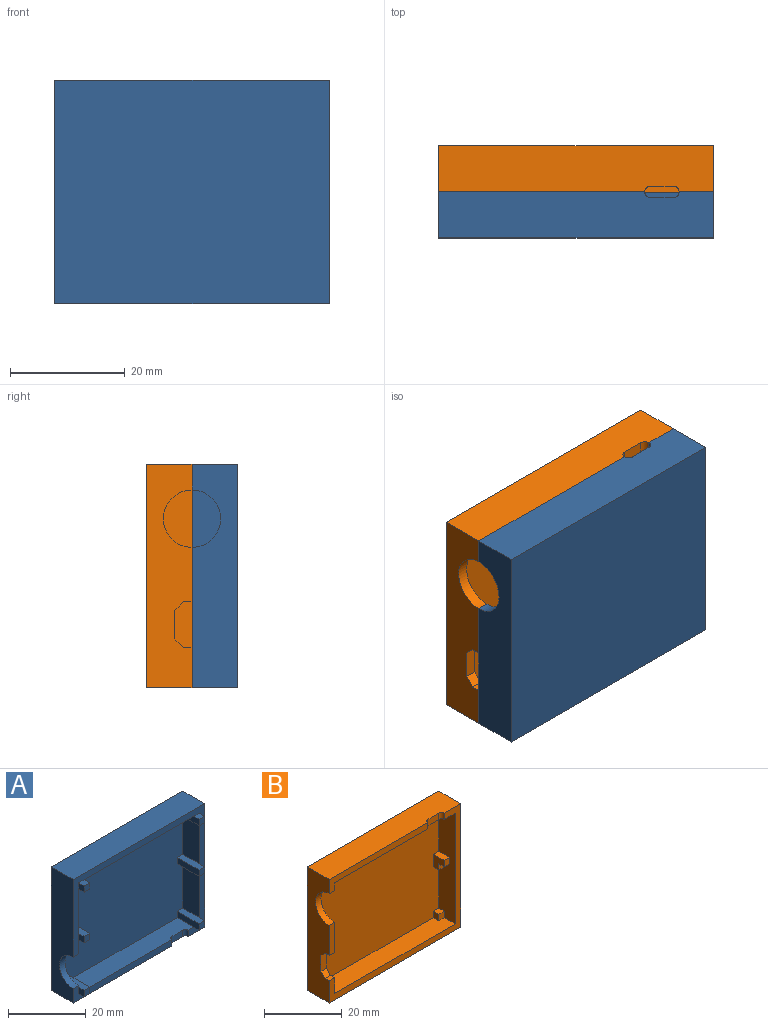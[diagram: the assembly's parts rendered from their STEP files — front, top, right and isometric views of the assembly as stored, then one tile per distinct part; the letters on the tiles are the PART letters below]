
ASSEMBLY  parts=2 mates=1
PART A: 48 faces, bbox 48x10x39 mm
  f0: plane 48x39mm, normal (0,-1,0), area 223mm2, adj f2,f3,f4,f5,f6,f7,f8,f9
  f1: plane 44x35mm, normal (0,-1,0), area 1516mm2, adj f2,f3,f4,f5,f6,f7,f16,f17
  f2: plane 40x6mm, normal (0,0,1), area 234.4mm2, adj f0,f1,f13,f38,f42,f45,f46,f47
  f3: plane 15x6mm, normal (1,0,0), area 50.7mm2, adj f0,f1,f13,f14,f31,f35
  f4: plane 15x6mm, normal (-1,0,0), area 90mm2, adj f0,f1,f26,f41
  f5: plane 40x6mm, normal (0,0,-1), area 240mm2, adj f0,f1,f17,f20
  f6: plane 14x6mm, normal (-1,0,0), area 84mm2, adj f0,f1,f21,f27
  f7: plane 14x6mm, normal (1,0,0), area 84mm2, adj f0,f1,f16,f33
  f8: plane 39x8mm, normal (-1,0,0), area 272.7mm2, adj f0,f9,f11,f12,f13,f14
  f9: plane 48x8mm, normal (0,0,-1), area 378.4mm2, adj f0,f8,f10,f12,f13,f45,f46,f47
  f10: plane 39x8mm, normal (1,0,0), area 312mm2, adj f0,f9,f11,f12
  f11: plane 48x8mm, normal (0,0,1), area 384mm2, adj f0,f8,f10,f12
  f12: plane 48x39mm, normal (0,1,0), area 1872mm2, adj f8,f9,f10,f11
  f13: plane 36x4.5mm, normal (0,-1,0), area 77mm2, adj f2,f3,f8,f9,f14,f36,f37,f47
  f14: cylinder r=5mm len=10mm, axis (-1,0,0), area 31.4mm2, adj f0,f3,f8,f13
  f15: plane 2x2mm, normal (-1,0,0), area 4mm2, adj f0,f16,f18,f19
  f16: plane 8x2mm, normal (0,0,-1), area 16mm2, adj f1,f7,f15,f17,f19
  f17: plane 8x2mm, normal (1,0,0), area 16mm2, adj f1,f5,f16,f18,f19
  f18: plane 2x2mm, normal (0,0,1), area 4mm2, adj f0,f15,f17,f19
  f19: plane 2x2mm, normal (0,-1,0), area 4mm2, adj f15,f16,f17,f18
  f20: plane 8x2mm, normal (-1,0,0), area 16mm2, adj f1,f5,f21,f23,f24
  f21: plane 8x2mm, normal (0,0,-1), area 16mm2, adj f1,f6,f20,f22,f24
  f22: plane 2x2mm, normal (1,0,0), area 4mm2, adj f0,f21,f23,f24
  f23: plane 2x2mm, normal (0,0,1), area 4mm2, adj f0,f20,f22,f24
  f24: plane 2x2mm, normal (0,-1,0), area 4mm2, adj f20,f21,f22,f23
  f25: plane 2x2mm, normal (1,0,0), area 4mm2, adj f0,f26,f27,f29
  f26: plane 8x2mm, normal (0,0,-1), area 16mm2, adj f1,f4,f25,f28,f29
  f27: plane 8x2mm, normal (0,0,1), area 16mm2, adj f1,f6,f25,f28,f29
  f28: plane 8x2mm, normal (-1,0,0), area 16mm2, adj f1,f26,f27,f29
  f29: plane 2x2mm, normal (0,-1,0), area 4mm2, adj f25,f26,f27,f28
  f30: plane 2x2mm, normal (-1,0,0), area 4mm2, adj f0,f31,f33,f34
  f31: plane 8x2mm, normal (0,0,-1), area 16mm2, adj f1,f3,f30,f32,f34
  f32: plane 8x2mm, normal (1,0,0), area 16mm2, adj f1,f31,f33,f34
  f33: plane 8x2mm, normal (0,0,1), area 16mm2, adj f1,f7,f30,f32,f34
  f34: plane 2x2mm, normal (0,-1,0), area 4mm2, adj f30,f31,f32,f33
  f35: plane 8x2mm, normal (0,0,1), area 16mm2, adj f1,f3,f36,f38,f39
  f36: plane 2x2mm, normal (-1,0,0), area 4mm2, adj f13,f35,f37,f39
  f37: plane 2x2mm, normal (0,0,-1), area 4mm2, adj f13,f36,f38,f39
  f38: plane 8x2mm, normal (1,0,0), area 16mm2, adj f1,f2,f35,f37,f39
  f39: plane 2x2mm, normal (0,-1,0), area 4mm2, adj f35,f36,f37,f38
  f40: plane 2x2mm, normal (1,0,0), area 4mm2, adj f0,f41,f43,f44
  f41: plane 8x2mm, normal (0,0,1), area 16mm2, adj f1,f4,f40,f42,f44
  f42: plane 8x2mm, normal (-1,0,0), area 16mm2, adj f1,f2,f41,f43,f44
  f43: plane 2x2mm, normal (0,0,-1), area 4mm2, adj f0,f40,f42,f44
  f44: plane 2x2mm, normal (0,-1,0), area 4mm2, adj f40,f41,f42,f43
  f45: plane 4x2mm, normal (0,-1,0), area 8mm2, adj f2,f9,f46,f47
  f46: cylinder r=1mm len=2mm, axis (0,0,1), area 3.1mm2, adj f0,f2,f9,f45
  f47: cylinder r=1mm len=2mm, axis (0,0,-1), area 3.1mm2, adj f2,f9,f13,f45
PART B: 40 faces, bbox 48x8x39 mm
  f0: plane 36x4.5mm, normal (0,-1,0), area 77mm2, adj f4,f5,f7,f11,f16,f39
  f1: plane 35x6mm, normal (-1,0,0), area 194mm2, adj f2,f6,f11,f12,f24,f26,f27,f29
  f2: plane 44x35mm, normal (0,-1,0), area 1516mm2, adj f1,f4,f11,f12,f17,f18,f20,f21
  f3: plane 9.5x2mm, normal (0,-1,0), area 19mm2, adj f4,f5,f14,f16
  f4: plane 35x6mm, normal (1,0,0), area 133mm2, adj f0,f2,f3,f6,f11,f12,f13,f14
  f5: plane 39x8mm, normal (-1,0,0), area 251mm2, adj f0,f3,f6,f7,f8,f10,f13,f14
  f6: plane 48x39mm, normal (0,-1,0), area 188mm2, adj f1,f4,f5,f7,f8,f9,f11,f12
  f7: plane 48x8mm, normal (0,0,1), area 378.4mm2, adj f0,f5,f6,f9,f10,f37,f38,f39
  f8: plane 48x8mm, normal (0,0,-1), area 384mm2, adj f5,f6,f9,f10
  f9: plane 39x8mm, normal (1,0,0), area 312mm2, adj f6,f7,f8,f10
  f10: plane 48x39mm, normal (0,1,0), area 1872mm2, adj f5,f7,f8,f9
  f11: plane 44x6mm, normal (0,0,-1), area 258.4mm2, adj f0,f1,f2,f4,f6,f37,f38,f39
  f12: plane 44x6mm, normal (0,0,1), area 256mm2, adj f1,f2,f4,f6,f18,f19,f25,f26
  f13: plane 2x1.5mm, normal (0,0,1), area 3mm2, adj f4,f5,f6,f35
  f14: plane 2x1.5mm, normal (0,0,-1), area 3mm2, adj f3,f4,f5,f36
  f15: plane 5x2mm, normal (0,-1,0), area 10mm2, adj f4,f5,f35,f36
  f16: cylinder r=5mm len=10mm, axis (-1,0,0), area 31.4mm2, adj f0,f3,f4,f5
  f17: plane 2x2mm, normal (0,0,1), area 4mm2, adj f2,f4,f18,f19
  f18: plane 2x2mm, normal (1,0,0), area 4mm2, adj f2,f12,f17,f19
  f19: plane 2x2mm, normal (0,-1,0), area 4mm2, adj f4,f12,f17,f18
  f20: plane 4x2mm, normal (0,0,1), area 8mm2, adj f2,f4,f22,f32
  f21: plane 2x2mm, normal (0,0,-1), area 4mm2, adj f2,f4,f22,f23
  f22: plane 4x4mm, normal (1,0,0), area 12mm2, adj f2,f20,f21,f23,f31,f32
  f23: plane 2x2mm, normal (0,-1,0), area 4mm2, adj f4,f21,f22,f31
  f24: plane 2x2mm, normal (0,0,1), area 4mm2, adj f1,f2,f25,f26
  f25: plane 2x2mm, normal (-1,0,0), area 4mm2, adj f2,f12,f24,f26
  f26: plane 2x2mm, normal (0,-1,0), area 4mm2, adj f1,f12,f24,f25
  f27: plane 4x2mm, normal (0,0,1), area 8mm2, adj f1,f2,f28,f34
  f28: plane 4x4mm, normal (-1,0,0), area 12mm2, adj f2,f27,f29,f30,f33,f34
  f29: plane 2x2mm, normal (0,0,-1), area 4mm2, adj f1,f2,f28,f30
  f30: plane 2x2mm, normal (0,-1,0), area 4mm2, adj f1,f28,f29,f33
  f31: plane 2x2mm, normal (0,0,-1), area 4mm2, adj f4,f22,f23,f32
  f32: plane 2x2mm, normal (0,-1,0), area 4mm2, adj f4,f20,f22,f31
  f33: plane 2x2mm, normal (0,0,-1), area 4mm2, adj f1,f28,f30,f34
  f34: plane 2x2mm, normal (0,-1,0), area 4mm2, adj f1,f27,f28,f33
  f35: plane 2x1.5mm, normal (0,-0.71,0.71), area 4.2mm2, adj f4,f5,f13,f15
  f36: plane 2x1.5mm, normal (0,-0.71,-0.71), area 4.2mm2, adj f4,f5,f14,f15
  f37: plane 4x2mm, normal (0,-1,0), area 8mm2, adj f7,f11,f38,f39
  f38: cylinder r=1mm len=2mm, axis (0,0,-1), area 3.1mm2, adj f6,f7,f11,f37
  f39: cylinder r=1mm len=2mm, axis (0,0,1), area 3.1mm2, adj f0,f7,f11,f37
PLACE A rot(axis=(1,0,0),180deg) t=(5.6,-38.87,44.09)mm
PLACE B t=(5.5,-22.87,-8.03)mm
MATE fastened A.f14 <-> B.f16  axis (-1,0,0) through (11.92,-30.87,29.52)mm
